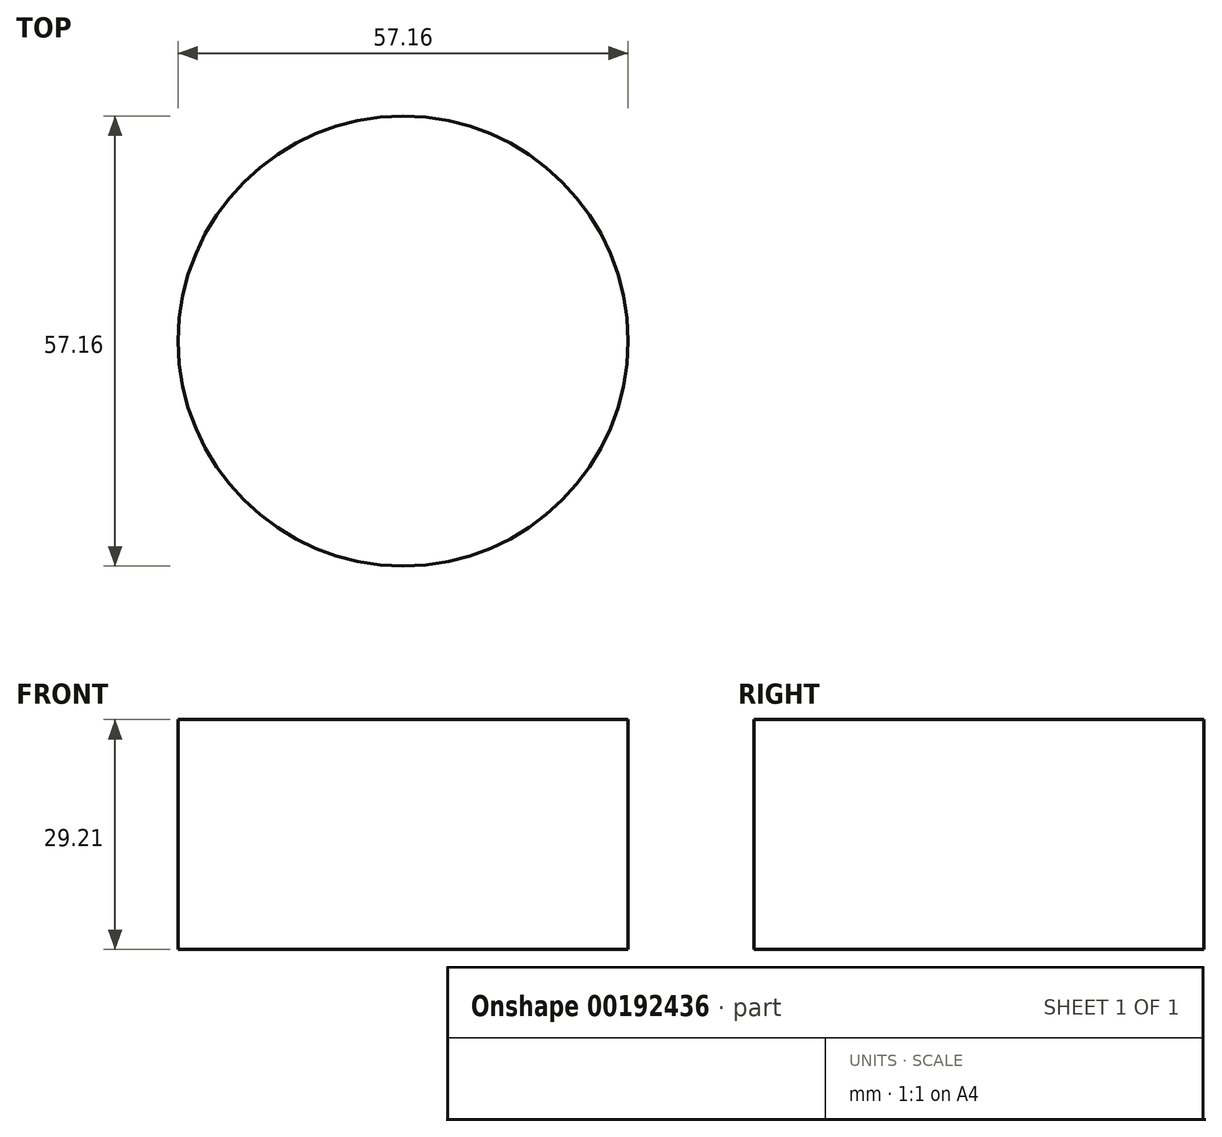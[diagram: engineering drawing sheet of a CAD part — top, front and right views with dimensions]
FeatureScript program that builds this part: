
annotation { "Feature Type Name" : "Feature", "Feature Type Description" : "" }
export const myFeature = defineFeature(function(context is Context, id is Id, definition is map)
    precondition{}
    {
        {
            var Q0;
            Q0=qCreatedBy(makeId("Top.planeOp"),FACE);
            var sketch = newSketch(context, id + "F0", { "sketchPlane" : qUnion([Q0])});
            skCircle(sketch, "E0", {"center": v(0, 0) * mm, "radius": 28.58 * mm});
            skSolve(sketch);
        }
        {
            var Q0;
            Q0 = qSketchRegion(id + "F0", true);
            extrude(context, id + "F1", {"entities" : qUnion([Q0]), "depth" : 29.2 * mm});
        }
    });
